# Revit family: NP15_100_200_2D
name_source: partatom
category: Detail Items
revit_build: Autodesk Revit 2014 (Build: 20130308_1515(x64)
units: mm (PartAtom-declared; Revit-internal decimal feet)

## types (4) — shared parameters
Date Last Modified = October 31, 2016
Description = Strap
Family Version = 1.0.0
Manufacturer = Simpson Strong-Tie Company Inc.
Model = NP15/100/200
Model Disclaimer = Contact Simpson Strong-Tie Company Inc. for more information
Product Type = Strap
Provide Feedback = http://www.strongtie.com
URL = www.strongtie.eu\s\NP

## per-type parameters (varying)
| type | Left View | Top View |
| Front View | No | No |
| Left View | Yes | No |
| Right View | No | No |
| Top View | No | Yes |

type visibility flags (boolean, named after types; folded from table):
- Front View: Yes: Front View
- Left View: Yes: (none)
- Right View: Yes: Right View
- Top View: Yes: (none)

## geometry (parser evidence)
native form markers: Sweep x1
no freeform markers — native parametric forms only
